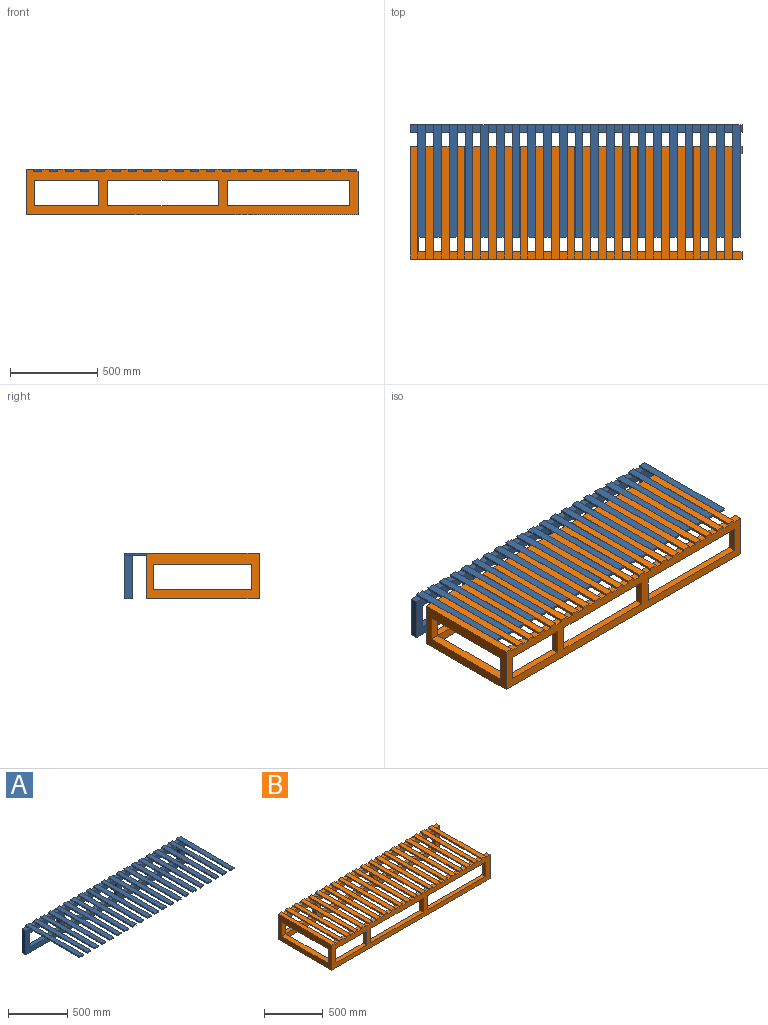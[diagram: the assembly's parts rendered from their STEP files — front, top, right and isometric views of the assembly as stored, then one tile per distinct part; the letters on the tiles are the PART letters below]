
ASSEMBLY  parts=2 mates=1
PART A: 144 faces, bbox 1900x644x262 mm
  f0: plane 46x41mm, normal (0,0,1), area 1886mm2, adj f37,f38,f136,f142
  f1: plane 46x41mm, normal (0,0,1), area 1886mm2, adj f37,f38,f131,f137
  f2: plane 46x41mm, normal (0,0,1), area 1886mm2, adj f37,f38,f126,f132
  f3: plane 46x41mm, normal (0,0,1), area 1886mm2, adj f37,f38,f121,f127
  f4: plane 46x41mm, normal (0,0,1), area 1886mm2, adj f37,f38,f116,f122
  f5: plane 46x41mm, normal (0,0,1), area 1886mm2, adj f37,f38,f111,f117
  f6: plane 46x41mm, normal (0,0,1), area 1886mm2, adj f37,f38,f106,f112
  f7: plane 46x41mm, normal (0,0,1), area 1886mm2, adj f37,f38,f101,f107
  f8: plane 46x41mm, normal (0,0,1), area 1886mm2, adj f37,f38,f96,f102
  f9: plane 46x41mm, normal (0,0,1), area 1886mm2, adj f37,f38,f91,f97
  f10: plane 46x41mm, normal (0,0,1), area 1886mm2, adj f37,f38,f86,f92
  f11: plane 46x41mm, normal (0,0,1), area 1886mm2, adj f37,f38,f81,f87
  f12: plane 46x41mm, normal (0,0,1), area 1886mm2, adj f37,f38,f76,f82
  f13: plane 46x41mm, normal (0,0,1), area 1886mm2, adj f37,f38,f71,f77
  f14: plane 46x41mm, normal (0,0,1), area 1886mm2, adj f37,f38,f66,f72
  f15: plane 46x41mm, normal (0,0,1), area 1886mm2, adj f37,f38,f61,f67
  f16: plane 46x41mm, normal (0,0,1), area 1886mm2, adj f37,f38,f56,f62
  f17: plane 46x41mm, normal (0,0,1), area 1886mm2, adj f37,f38,f51,f57
  f18: plane 46x41mm, normal (0,0,1), area 1886mm2, adj f37,f38,f46,f52
  f19: plane 46x41mm, normal (0,0,1), area 1886mm2, adj f37,f38,f41,f47
  f20: plane 45x41mm, normal (0,0,1), area 1845mm2, adj f31,f37,f38,f42
  f21: plane 630.94x41mm, normal (0,0,1), area 25868.7mm2, adj f22,f36,f37,f38
  f22: plane 148x41mm, normal (-1,0,0), area 6068mm2, adj f21,f23,f37,f38
  f23: plane 630.94x41mm, normal (0,0,-1), area 25868.7mm2, adj f22,f36,f37,f38
  f24: plane 148x41mm, normal (-1,0,0), area 6068mm2, adj f25,f33,f37,f38
  f25: plane 698.47x41mm, normal (0,0,-1), area 28637.4mm2, adj f24,f26,f37,f38
  f26: plane 148x41mm, normal (1,0,0), area 6068mm2, adj f25,f33,f37,f38
  f27: plane 148x41mm, normal (1,0,0), area 6068mm2, adj f28,f34,f37,f38
  f28: plane 366.58x41mm, normal (0,0,1), area 15029.9mm2, adj f27,f29,f37,f38
  f29: plane 148x41mm, normal (-1,0,0), area 6068mm2, adj f28,f34,f37,f38
  f30: plane 1900x41mm, normal (0,0,-1), area 77900mm2, adj f31,f35,f37,f38
  f31: plane 250x41mm, normal (-1,0,0), area 10250mm2, adj f20,f30,f37,f38
  f32: plane 41x11mm, normal (0,0,1), area 451mm2, adj f35,f37,f38,f141
  f33: plane 698.47x41mm, normal (0,0,1), area 28637.4mm2, adj f24,f26,f37,f38
  f34: plane 366.58x41mm, normal (0,0,-1), area 15029.9mm2, adj f27,f29,f37,f38
  f35: plane 250x41mm, normal (1,0,0), area 10250mm2, adj f30,f32,f37,f38
  f36: plane 148x41mm, normal (1,0,0), area 6068mm2, adj f21,f23,f37,f38
  f37: plane 1900x262mm, normal (0,1,0), area 235080mm2, adj f0,f1,f2,f3,f4,f5,f6,f7
  f38: plane 1900x250mm, normal (0,-1,0), area 223992mm2, adj f0,f1,f2,f3,f4,f5,f6,f7
  f39: plane 603x44mm, normal (0,0,-1), area 26532mm2, adj f38,f41,f42,f43
  f40: plane 644x44mm, normal (0,0,1), area 28336mm2, adj f37,f41,f42,f43
  f41: plane 644x12mm, normal (1,0,0), area 7728mm2, adj f19,f37,f39,f40,f43
  f42: plane 644x12mm, normal (-1,0,0), area 7728mm2, adj f20,f37,f39,f40,f43
  f43: plane 44x12mm, normal (0,-1,0), area 528mm2, adj f39,f40,f41,f42
  f44: plane 603x44mm, normal (0,0,-1), area 26532mm2, adj f38,f46,f47,f48
  f45: plane 644x44mm, normal (0,0,1), area 28336mm2, adj f37,f46,f47,f48
  f46: plane 644x12mm, normal (1,0,0), area 7728mm2, adj f18,f37,f44,f45,f48
  f47: plane 644x12mm, normal (-1,0,0), area 7728mm2, adj f19,f37,f44,f45,f48
  f48: plane 44x12mm, normal (0,-1,0), area 528mm2, adj f44,f45,f46,f47
  f49: plane 603x44mm, normal (0,0,-1), area 26532mm2, adj f38,f51,f52,f53
  f50: plane 644x44mm, normal (0,0,1), area 28336mm2, adj f37,f51,f52,f53
  f51: plane 644x12mm, normal (1,0,0), area 7728mm2, adj f17,f37,f49,f50,f53
  f52: plane 644x12mm, normal (-1,0,0), area 7728mm2, adj f18,f37,f49,f50,f53
  f53: plane 44x12mm, normal (0,-1,0), area 528mm2, adj f49,f50,f51,f52
  f54: plane 603x44mm, normal (0,0,-1), area 26532mm2, adj f38,f56,f57,f58
  f55: plane 644x44mm, normal (0,0,1), area 28336mm2, adj f37,f56,f57,f58
  f56: plane 644x12mm, normal (1,0,0), area 7728mm2, adj f16,f37,f54,f55,f58
  f57: plane 644x12mm, normal (-1,0,0), area 7728mm2, adj f17,f37,f54,f55,f58
  f58: plane 44x12mm, normal (0,-1,0), area 528mm2, adj f54,f55,f56,f57
  f59: plane 603x44mm, normal (0,0,-1), area 26532mm2, adj f38,f61,f62,f63
  f60: plane 644x44mm, normal (0,0,1), area 28336mm2, adj f37,f61,f62,f63
  f61: plane 644x12mm, normal (1,0,0), area 7728mm2, adj f15,f37,f59,f60,f63
  f62: plane 644x12mm, normal (-1,0,0), area 7728mm2, adj f16,f37,f59,f60,f63
  f63: plane 44x12mm, normal (0,-1,0), area 528mm2, adj f59,f60,f61,f62
  f64: plane 603x44mm, normal (0,0,-1), area 26532mm2, adj f38,f66,f67,f68
  f65: plane 644x44mm, normal (0,0,1), area 28336mm2, adj f37,f66,f67,f68
  f66: plane 644x12mm, normal (1,0,0), area 7728mm2, adj f14,f37,f64,f65,f68
  f67: plane 644x12mm, normal (-1,0,0), area 7728mm2, adj f15,f37,f64,f65,f68
  f68: plane 44x12mm, normal (0,-1,0), area 528mm2, adj f64,f65,f66,f67
  f69: plane 603x44mm, normal (0,0,-1), area 26532mm2, adj f38,f71,f72,f73
  f70: plane 644x44mm, normal (0,0,1), area 28336mm2, adj f37,f71,f72,f73
  f71: plane 644x12mm, normal (1,0,0), area 7728mm2, adj f13,f37,f69,f70,f73
  f72: plane 644x12mm, normal (-1,0,0), area 7728mm2, adj f14,f37,f69,f70,f73
  f73: plane 44x12mm, normal (0,-1,0), area 528mm2, adj f69,f70,f71,f72
  f74: plane 603x44mm, normal (0,0,-1), area 26532mm2, adj f38,f76,f77,f78
  f75: plane 644x44mm, normal (0,0,1), area 28336mm2, adj f37,f76,f77,f78
  f76: plane 644x12mm, normal (1,0,0), area 7728mm2, adj f12,f37,f74,f75,f78
  f77: plane 644x12mm, normal (-1,0,0), area 7728mm2, adj f13,f37,f74,f75,f78
  f78: plane 44x12mm, normal (0,-1,0), area 528mm2, adj f74,f75,f76,f77
  f79: plane 603x44mm, normal (0,0,-1), area 26532mm2, adj f38,f81,f82,f83
  f80: plane 644x44mm, normal (0,0,1), area 28336mm2, adj f37,f81,f82,f83
  f81: plane 644x12mm, normal (1,0,0), area 7728mm2, adj f11,f37,f79,f80,f83
  f82: plane 644x12mm, normal (-1,0,0), area 7728mm2, adj f12,f37,f79,f80,f83
  f83: plane 44x12mm, normal (0,-1,0), area 528mm2, adj f79,f80,f81,f82
  f84: plane 603x44mm, normal (0,0,-1), area 26532mm2, adj f38,f86,f87,f88
  f85: plane 644x44mm, normal (0,0,1), area 28336mm2, adj f37,f86,f87,f88
  f86: plane 644x12mm, normal (1,0,0), area 7728mm2, adj f10,f37,f84,f85,f88
  f87: plane 644x12mm, normal (-1,0,0), area 7728mm2, adj f11,f37,f84,f85,f88
  f88: plane 44x12mm, normal (0,-1,0), area 528mm2, adj f84,f85,f86,f87
  f89: plane 603x44mm, normal (0,0,-1), area 26532mm2, adj f38,f91,f92,f93
  f90: plane 644x44mm, normal (0,0,1), area 28336mm2, adj f37,f91,f92,f93
  f91: plane 644x12mm, normal (1,0,0), area 7728mm2, adj f9,f37,f89,f90,f93
  f92: plane 644x12mm, normal (-1,0,0), area 7728mm2, adj f10,f37,f89,f90,f93
  f93: plane 44x12mm, normal (0,-1,0), area 528mm2, adj f89,f90,f91,f92
  f94: plane 603x44mm, normal (0,0,-1), area 26532mm2, adj f38,f96,f97,f98
  f95: plane 644x44mm, normal (0,0,1), area 28336mm2, adj f37,f96,f97,f98
  f96: plane 644x12mm, normal (1,0,0), area 7728mm2, adj f8,f37,f94,f95,f98
  f97: plane 644x12mm, normal (-1,0,0), area 7728mm2, adj f9,f37,f94,f95,f98
  f98: plane 44x12mm, normal (0,-1,0), area 528mm2, adj f94,f95,f96,f97
  f99: plane 603x44mm, normal (0,0,-1), area 26532mm2, adj f38,f101,f102,f103
  f100: plane 644x44mm, normal (0,0,1), area 28336mm2, adj f37,f101,f102,f103
  f101: plane 644x12mm, normal (1,0,0), area 7728mm2, adj f7,f37,f99,f100,f103
  f102: plane 644x12mm, normal (-1,0,0), area 7728mm2, adj f8,f37,f99,f100,f103
  f103: plane 44x12mm, normal (0,-1,0), area 528mm2, adj f99,f100,f101,f102
  f104: plane 603x44mm, normal (0,0,-1), area 26532mm2, adj f38,f106,f107,f108
  f105: plane 644x44mm, normal (0,0,1), area 28336mm2, adj f37,f106,f107,f108
  f106: plane 644x12mm, normal (1,0,0), area 7728mm2, adj f6,f37,f104,f105,f108
  f107: plane 644x12mm, normal (-1,0,0), area 7728mm2, adj f7,f37,f104,f105,f108
  f108: plane 44x12mm, normal (0,-1,0), area 528mm2, adj f104,f105,f106,f107
  f109: plane 603x44mm, normal (0,0,-1), area 26532mm2, adj f38,f111,f112,f113
  f110: plane 644x44mm, normal (0,0,1), area 28336mm2, adj f37,f111,f112,f113
  f111: plane 644x12mm, normal (1,0,0), area 7728mm2, adj f5,f37,f109,f110,f113
  f112: plane 644x12mm, normal (-1,0,0), area 7728mm2, adj f6,f37,f109,f110,f113
  f113: plane 44x12mm, normal (0,-1,0), area 528mm2, adj f109,f110,f111,f112
  f114: plane 603x44mm, normal (0,0,-1), area 26532mm2, adj f38,f116,f117,f118
  f115: plane 644x44mm, normal (0,0,1), area 28336mm2, adj f37,f116,f117,f118
  f116: plane 644x12mm, normal (1,0,0), area 7728mm2, adj f4,f37,f114,f115,f118
  f117: plane 644x12mm, normal (-1,0,0), area 7728mm2, adj f5,f37,f114,f115,f118
  f118: plane 44x12mm, normal (0,-1,0), area 528mm2, adj f114,f115,f116,f117
  f119: plane 603x44mm, normal (0,0,-1), area 26532mm2, adj f38,f121,f122,f123
  f120: plane 644x44mm, normal (0,0,1), area 28336mm2, adj f37,f121,f122,f123
  f121: plane 644x12mm, normal (1,0,0), area 7728mm2, adj f3,f37,f119,f120,f123
  f122: plane 644x12mm, normal (-1,0,0), area 7728mm2, adj f4,f37,f119,f120,f123
  f123: plane 44x12mm, normal (0,-1,0), area 528mm2, adj f119,f120,f121,f122
  f124: plane 603x44mm, normal (0,0,-1), area 26532mm2, adj f38,f126,f127,f128
  f125: plane 644x44mm, normal (0,0,1), area 28336mm2, adj f37,f126,f127,f128
  f126: plane 644x12mm, normal (1,0,0), area 7728mm2, adj f2,f37,f124,f125,f128
  f127: plane 644x12mm, normal (-1,0,0), area 7728mm2, adj f3,f37,f124,f125,f128
  f128: plane 44x12mm, normal (0,-1,0), area 528mm2, adj f124,f125,f126,f127
  f129: plane 603x44mm, normal (0,0,-1), area 26532mm2, adj f38,f131,f132,f133
  f130: plane 644x44mm, normal (0,0,1), area 28336mm2, adj f37,f131,f132,f133
  f131: plane 644x12mm, normal (1,0,0), area 7728mm2, adj f1,f37,f129,f130,f133
  f132: plane 644x12mm, normal (-1,0,0), area 7728mm2, adj f2,f37,f129,f130,f133
  f133: plane 44x12mm, normal (0,-1,0), area 528mm2, adj f129,f130,f131,f132
  f134: plane 603x44mm, normal (0,0,-1), area 26532mm2, adj f38,f136,f137,f138
  f135: plane 644x44mm, normal (0,0,1), area 28336mm2, adj f37,f136,f137,f138
  f136: plane 644x12mm, normal (1,0,0), area 7728mm2, adj f0,f37,f134,f135,f138
  f137: plane 644x12mm, normal (-1,0,0), area 7728mm2, adj f1,f37,f134,f135,f138
  f138: plane 44x12mm, normal (0,-1,0), area 528mm2, adj f134,f135,f136,f137
  f139: plane 603x44mm, normal (0,0,-1), area 26532mm2, adj f38,f141,f142,f143
  f140: plane 644x44mm, normal (0,0,1), area 28336mm2, adj f37,f141,f142,f143
  f141: plane 644x12mm, normal (1,0,0), area 7728mm2, adj f32,f37,f139,f140,f143
  f142: plane 644x12mm, normal (-1,0,0), area 7728mm2, adj f0,f37,f139,f140,f143
  f143: plane 44x12mm, normal (0,-1,0), area 528mm2, adj f139,f140,f141,f142
PART B: 161 faces, bbox 1900x644x262 mm
  f0: plane 46x41mm, normal (0,0,1), area 1886mm2, adj f41,f58,f154,f159
  f1: plane 56x41mm, normal (0,0,1), area 2296mm2, adj f41,f56,f58,f158
  f2: plane 46x41mm, normal (0,0,1), area 1886mm2, adj f59,f74,f154,f159
  f3: plane 56x41mm, normal (0,0,1), area 2296mm2, adj f59,f72,f74,f158
  f4: plane 46x41mm, normal (0,0,1), area 1886mm2, adj f41,f58,f150,f155
  f5: plane 46x41mm, normal (0,0,1), area 1886mm2, adj f59,f74,f150,f155
  f6: plane 46x41mm, normal (0,0,1), area 1886mm2, adj f41,f58,f146,f151
  f7: plane 46x41mm, normal (0,0,1), area 1886mm2, adj f59,f74,f146,f151
  f8: plane 46x41mm, normal (0,0,1), area 1886mm2, adj f41,f58,f142,f147
  f9: plane 46x41mm, normal (0,0,1), area 1886mm2, adj f59,f74,f142,f147
  f10: plane 46x41mm, normal (0,0,1), area 1886mm2, adj f41,f58,f138,f143
  f11: plane 46x41mm, normal (0,0,1), area 1886mm2, adj f59,f74,f138,f143
  f12: plane 46x41mm, normal (0,0,1), area 1886mm2, adj f41,f58,f134,f139
  f13: plane 46x41mm, normal (0,0,1), area 1886mm2, adj f59,f74,f134,f139
  f14: plane 46x41mm, normal (0,0,1), area 1886mm2, adj f41,f58,f130,f135
  f15: plane 46x41mm, normal (0,0,1), area 1886mm2, adj f59,f74,f130,f135
  f16: plane 46x41mm, normal (0,0,1), area 1886mm2, adj f41,f58,f126,f131
  f17: plane 46x41mm, normal (0,0,1), area 1886mm2, adj f59,f74,f126,f131
  f18: plane 46x41mm, normal (0,0,1), area 1886mm2, adj f41,f58,f122,f127
  f19: plane 46x41mm, normal (0,0,1), area 1886mm2, adj f59,f74,f122,f127
  f20: plane 46x41mm, normal (0,0,1), area 1886mm2, adj f41,f58,f118,f123
  f21: plane 46x41mm, normal (0,0,1), area 1886mm2, adj f59,f74,f118,f123
  f22: plane 46x41mm, normal (0,0,1), area 1886mm2, adj f41,f58,f114,f119
  f23: plane 46x41mm, normal (0,0,1), area 1886mm2, adj f59,f74,f114,f119
  f24: plane 46x41mm, normal (0,0,1), area 1886mm2, adj f41,f58,f110,f115
  f25: plane 46x41mm, normal (0,0,1), area 1886mm2, adj f59,f74,f110,f115
  f26: plane 46x41mm, normal (0,0,1), area 1886mm2, adj f41,f58,f106,f111
  f27: plane 46x41mm, normal (0,0,1), area 1886mm2, adj f59,f74,f106,f111
  f28: plane 46x41mm, normal (0,0,1), area 1886mm2, adj f41,f58,f102,f107
  f29: plane 46x41mm, normal (0,0,1), area 1886mm2, adj f59,f74,f102,f107
  f30: plane 46x41mm, normal (0,0,1), area 1886mm2, adj f41,f58,f98,f103
  f31: plane 46x41mm, normal (0,0,1), area 1886mm2, adj f59,f74,f98,f103
  f32: plane 46x41mm, normal (0,0,1), area 1886mm2, adj f41,f58,f94,f99
  f33: plane 46x41mm, normal (0,0,1), area 1886mm2, adj f59,f74,f94,f99
  f34: plane 46x41mm, normal (0,0,1), area 1886mm2, adj f41,f58,f90,f95
  f35: plane 46x41mm, normal (0,0,1), area 1886mm2, adj f59,f74,f90,f95
  f36: plane 46x41mm, normal (0,0,1), area 1886mm2, adj f41,f58,f86,f91
  f37: plane 46x41mm, normal (0,0,1), area 1886mm2, adj f59,f74,f86,f91
  f38: plane 46x41mm, normal (0,0,1), area 1886mm2, adj f41,f58,f82,f87
  f39: plane 46x41mm, normal (0,0,1), area 1886mm2, adj f59,f74,f82,f87
  f40: plane 644x46mm, normal (0,0,1), area 7706mm2, adj f41,f58,f59,f74,f75,f79,f83
  f41: plane 1849x250mm, normal (0,1,0), area 211242mm2, adj f0,f1,f4,f6,f8,f10,f12,f14
  f42: plane 148x51mm, normal (0,1,0), area 7548mm2, adj f49,f53,f76,f78
  f43: plane 630.94x41mm, normal (0,0,1), area 25868.7mm2, adj f41,f44,f57,f58
  f44: plane 148x41mm, normal (-1,0,0), area 6068mm2, adj f41,f43,f45,f58
  f45: plane 630.94x41mm, normal (0,0,-1), area 25868.7mm2, adj f41,f44,f57,f58
  f46: plane 148x41mm, normal (-1,0,0), area 6068mm2, adj f41,f47,f54,f58
  f47: plane 698.47x41mm, normal (0,0,-1), area 28637.4mm2, adj f41,f46,f48,f58
  f48: plane 148x41mm, normal (1,0,0), area 6068mm2, adj f41,f47,f54,f58
  f49: plane 148x41mm, normal (1,0,0), area 6068mm2, adj f42,f50,f55,f58
  f50: plane 366.58x41mm, normal (0,0,1), area 15029.9mm2, adj f41,f49,f51,f58
  f51: plane 148x41mm, normal (-1,0,0), area 6068mm2, adj f41,f50,f55,f58
  f52: plane 1900x644mm, normal (0,0,-1), area 184462mm2, adj f41,f53,f56,f58,f59,f72,f74,f77
  f53: plane 644x262mm, normal (-1,0,0), area 85552mm2, adj f42,f52,f58,f60,f74,f76,f78,f80
  f54: plane 698.47x41mm, normal (0,0,1), area 28637.4mm2, adj f41,f46,f48,f58
  f55: plane 366.58x41mm, normal (0,0,-1), area 15029.9mm2, adj f41,f49,f51,f58
  f56: plane 250x41mm, normal (1,0,0), area 10250mm2, adj f1,f41,f52,f58
  f57: plane 148x41mm, normal (1,0,0), area 6068mm2, adj f41,f43,f45,f58
  f58: plane 1900x262mm, normal (0,-1,0), area 235080mm2, adj f0,f1,f4,f6,f8,f10,f12,f14
  f59: plane 1849x250mm, normal (0,-1,0), area 211242mm2, adj f2,f3,f5,f7,f9,f11,f13,f15
  f60: plane 148x51mm, normal (0,-1,0), area 7548mm2, adj f53,f67,f76,f78
  f61: plane 630.94x41mm, normal (0,0,1), area 25868.7mm2, adj f59,f62,f73,f74
  f62: plane 148x41mm, normal (-1,0,0), area 6068mm2, adj f59,f61,f63,f74
  f63: plane 630.94x41mm, normal (0,0,-1), area 25868.7mm2, adj f59,f62,f73,f74
  f64: plane 148x41mm, normal (-1,0,0), area 6068mm2, adj f59,f65,f70,f74
  f65: plane 698.47x41mm, normal (0,0,-1), area 28637.4mm2, adj f59,f64,f66,f74
  f66: plane 148x41mm, normal (1,0,0), area 6068mm2, adj f59,f65,f70,f74
  f67: plane 148x41mm, normal (1,0,0), area 6068mm2, adj f60,f68,f71,f74
  f68: plane 366.58x41mm, normal (0,0,1), area 15029.9mm2, adj f59,f67,f69,f74
  f69: plane 148x41mm, normal (-1,0,0), area 6068mm2, adj f59,f68,f71,f74
  f70: plane 698.47x41mm, normal (0,0,1), area 28637.4mm2, adj f59,f64,f66,f74
  f71: plane 366.58x41mm, normal (0,0,-1), area 15029.9mm2, adj f59,f67,f69,f74
  f72: plane 250x41mm, normal (1,0,0), area 10250mm2, adj f3,f52,f59,f74
  f73: plane 148x41mm, normal (1,0,0), area 6068mm2, adj f59,f61,f63,f74
  f74: plane 1900x262mm, normal (0,1,0), area 235080mm2, adj f2,f3,f5,f7,f9,f11,f13,f15
  f75: plane 562x51mm, normal (1,0,0), area 28662mm2, adj f40,f41,f59,f76
  f76: plane 562x51mm, normal (0,0,-1), area 28662mm2, adj f42,f53,f60,f75
  f77: plane 562x51mm, normal (1,0,0), area 28662mm2, adj f41,f52,f59,f78
  f78: plane 562x51mm, normal (0,0,1), area 28662mm2, adj f42,f53,f60,f77
  f79: plane 644x12mm, normal (1,0,0), area 7728mm2, adj f40,f58,f74,f80
  f80: plane 644x44mm, normal (0,0,1), area 28336mm2, adj f53,f58,f74,f79
  f81: plane 562x44mm, normal (0,0,-1), area 24728mm2, adj f41,f59,f82,f83
  f82: plane 644x12mm, normal (1,0,0), area 7728mm2, adj f38,f39,f58,f74,f81,f84
  f83: plane 644x12mm, normal (-1,0,0), area 7728mm2, adj f40,f58,f74,f81,f84
  f84: plane 644x44mm, normal (0,0,1), area 28336mm2, adj f58,f74,f82,f83
  f85: plane 562x44mm, normal (0,0,-1), area 24728mm2, adj f41,f59,f86,f87
  f86: plane 644x12mm, normal (1,0,0), area 7728mm2, adj f36,f37,f58,f74,f85,f88
  f87: plane 644x12mm, normal (-1,0,0), area 7728mm2, adj f38,f39,f58,f74,f85,f88
  f88: plane 644x44mm, normal (0,0,1), area 28336mm2, adj f58,f74,f86,f87
  f89: plane 562x44mm, normal (0,0,-1), area 24728mm2, adj f41,f59,f90,f91
  f90: plane 644x12mm, normal (1,0,0), area 7728mm2, adj f34,f35,f58,f74,f89,f92
  f91: plane 644x12mm, normal (-1,0,0), area 7728mm2, adj f36,f37,f58,f74,f89,f92
  f92: plane 644x44mm, normal (0,0,1), area 28336mm2, adj f58,f74,f90,f91
  f93: plane 562x44mm, normal (0,0,-1), area 24728mm2, adj f41,f59,f94,f95
  f94: plane 644x12mm, normal (1,0,0), area 7728mm2, adj f32,f33,f58,f74,f93,f96
  f95: plane 644x12mm, normal (-1,0,0), area 7728mm2, adj f34,f35,f58,f74,f93,f96
  f96: plane 644x44mm, normal (0,0,1), area 28336mm2, adj f58,f74,f94,f95
  f97: plane 562x44mm, normal (0,0,-1), area 24728mm2, adj f41,f59,f98,f99
  f98: plane 644x12mm, normal (1,0,0), area 7728mm2, adj f30,f31,f58,f74,f97,f100
  f99: plane 644x12mm, normal (-1,0,0), area 7728mm2, adj f32,f33,f58,f74,f97,f100
  f100: plane 644x44mm, normal (0,0,1), area 28336mm2, adj f58,f74,f98,f99
  f101: plane 562x44mm, normal (0,0,-1), area 24728mm2, adj f41,f59,f102,f103
  f102: plane 644x12mm, normal (1,0,0), area 7728mm2, adj f28,f29,f58,f74,f101,f104
  f103: plane 644x12mm, normal (-1,0,0), area 7728mm2, adj f30,f31,f58,f74,f101,f104
  f104: plane 644x44mm, normal (0,0,1), area 28336mm2, adj f58,f74,f102,f103
  f105: plane 562x44mm, normal (0,0,-1), area 24728mm2, adj f41,f59,f106,f107
  f106: plane 644x12mm, normal (1,0,0), area 7728mm2, adj f26,f27,f58,f74,f105,f108
  f107: plane 644x12mm, normal (-1,0,0), area 7728mm2, adj f28,f29,f58,f74,f105,f108
  f108: plane 644x44mm, normal (0,0,1), area 28336mm2, adj f58,f74,f106,f107
  f109: plane 562x44mm, normal (0,0,-1), area 24728mm2, adj f41,f59,f110,f111
  f110: plane 644x12mm, normal (1,0,0), area 7728mm2, adj f24,f25,f58,f74,f109,f112
  f111: plane 644x12mm, normal (-1,0,0), area 7728mm2, adj f26,f27,f58,f74,f109,f112
  f112: plane 644x44mm, normal (0,0,1), area 28336mm2, adj f58,f74,f110,f111
  f113: plane 562x44mm, normal (0,0,-1), area 24728mm2, adj f41,f59,f114,f115
  f114: plane 644x12mm, normal (1,0,0), area 7728mm2, adj f22,f23,f58,f74,f113,f116
  f115: plane 644x12mm, normal (-1,0,0), area 7728mm2, adj f24,f25,f58,f74,f113,f116
  f116: plane 644x44mm, normal (0,0,1), area 28336mm2, adj f58,f74,f114,f115
  f117: plane 562x44mm, normal (0,0,-1), area 24728mm2, adj f41,f59,f118,f119
  f118: plane 644x12mm, normal (1,0,0), area 7728mm2, adj f20,f21,f58,f74,f117,f120
  f119: plane 644x12mm, normal (-1,0,0), area 7728mm2, adj f22,f23,f58,f74,f117,f120
  f120: plane 644x44mm, normal (0,0,1), area 28336mm2, adj f58,f74,f118,f119
  f121: plane 562x44mm, normal (0,0,-1), area 24728mm2, adj f41,f59,f122,f123
  f122: plane 644x12mm, normal (1,0,0), area 7728mm2, adj f18,f19,f58,f74,f121,f124
  f123: plane 644x12mm, normal (-1,0,0), area 7728mm2, adj f20,f21,f58,f74,f121,f124
  f124: plane 644x44mm, normal (0,0,1), area 28336mm2, adj f58,f74,f122,f123
  f125: plane 562x44mm, normal (0,0,-1), area 24728mm2, adj f41,f59,f126,f127
  f126: plane 644x12mm, normal (1,0,0), area 7728mm2, adj f16,f17,f58,f74,f125,f128
  f127: plane 644x12mm, normal (-1,0,0), area 7728mm2, adj f18,f19,f58,f74,f125,f128
  f128: plane 644x44mm, normal (0,0,1), area 28336mm2, adj f58,f74,f126,f127
  f129: plane 562x44mm, normal (0,0,-1), area 24728mm2, adj f41,f59,f130,f131
  f130: plane 644x12mm, normal (1,0,0), area 7728mm2, adj f14,f15,f58,f74,f129,f132
  f131: plane 644x12mm, normal (-1,0,0), area 7728mm2, adj f16,f17,f58,f74,f129,f132
  f132: plane 644x44mm, normal (0,0,1), area 28336mm2, adj f58,f74,f130,f131
  f133: plane 562x44mm, normal (0,0,-1), area 24728mm2, adj f41,f59,f134,f135
  f134: plane 644x12mm, normal (1,0,0), area 7728mm2, adj f12,f13,f58,f74,f133,f136
  f135: plane 644x12mm, normal (-1,0,0), area 7728mm2, adj f14,f15,f58,f74,f133,f136
  f136: plane 644x44mm, normal (0,0,1), area 28336mm2, adj f58,f74,f134,f135
  f137: plane 562x44mm, normal (0,0,-1), area 24728mm2, adj f41,f59,f138,f139
  f138: plane 644x12mm, normal (1,0,0), area 7728mm2, adj f10,f11,f58,f74,f137,f140
  f139: plane 644x12mm, normal (-1,0,0), area 7728mm2, adj f12,f13,f58,f74,f137,f140
  f140: plane 644x44mm, normal (0,0,1), area 28336mm2, adj f58,f74,f138,f139
  f141: plane 562x44mm, normal (0,0,-1), area 24728mm2, adj f41,f59,f142,f143
  f142: plane 644x12mm, normal (1,0,0), area 7728mm2, adj f8,f9,f58,f74,f141,f144
  f143: plane 644x12mm, normal (-1,0,0), area 7728mm2, adj f10,f11,f58,f74,f141,f144
  f144: plane 644x44mm, normal (0,0,1), area 28336mm2, adj f58,f74,f142,f143
  f145: plane 562x44mm, normal (0,0,-1), area 24728mm2, adj f41,f59,f146,f147
  f146: plane 644x12mm, normal (1,0,0), area 7728mm2, adj f6,f7,f58,f74,f145,f148
  f147: plane 644x12mm, normal (-1,0,0), area 7728mm2, adj f8,f9,f58,f74,f145,f148
  f148: plane 644x44mm, normal (0,0,1), area 28336mm2, adj f58,f74,f146,f147
  f149: plane 562x44mm, normal (0,0,-1), area 24728mm2, adj f41,f59,f150,f151
  f150: plane 644x12mm, normal (1,0,0), area 7728mm2, adj f4,f5,f58,f74,f149,f152
  f151: plane 644x12mm, normal (-1,0,0), area 7728mm2, adj f6,f7,f58,f74,f149,f152
  f152: plane 644x44mm, normal (0,0,1), area 28336mm2, adj f58,f74,f150,f151
  f153: plane 562x44mm, normal (0,0,-1), area 24728mm2, adj f41,f59,f154,f155
  f154: plane 644x12mm, normal (1,0,0), area 7728mm2, adj f0,f2,f58,f74,f153,f156
  f155: plane 644x12mm, normal (-1,0,0), area 7728mm2, adj f4,f5,f58,f74,f153,f156
  f156: plane 644x44mm, normal (0,0,1), area 28336mm2, adj f58,f74,f154,f155
  f157: plane 562x44mm, normal (0,0,-1), area 24728mm2, adj f41,f59,f158,f159
  f158: plane 644x12mm, normal (1,0,0), area 7728mm2, adj f1,f3,f58,f74,f157,f160
  f159: plane 644x12mm, normal (-1,0,0), area 7728mm2, adj f0,f2,f58,f74,f157,f160
  f160: plane 644x44mm, normal (0,0,1), area 28336mm2, adj f58,f74,f158,f159
PLACE A t=(505,-474.49,0)mm
PLACE B t=(505,-39,0)mm
MATE slider B.f74 <-> A.f43  axis (0,1,0) through (67,0,250)mm
